# Revit family: Pump_Commercial-Effluent-Zoeller-180_Automatic_Series
name_source: partatom
category: Mechanical Equipment
revit_build: Autodesk Revit 2018 (Build: 20170223_1515(x64)
units: mm (PartAtom-declared; Revit-internal decimal feet)

## family parameters
Always vertical = No
Cut with Voids When Loaded = No
OmniClass Number = 23.60.30.21
OmniClass Title = Pumps
Part Type = Normal
Room Calculation Point = No
Round Connector Dimension = Use Radius
Shared = Yes
Work Plane-Based = Yes

## types (8) — shared parameters
Assembly Code = D2090
Cooling = Oil Filled
Cord Length = 240"
Cord Type = 1 Ph: UL listed 3-wire neoprene cord & plug
Default Elevation = 0"
Description = High Head Flow-Mate Series Submersible Effluent Pumps
Discharge Diameter = 1 1/2"
Discharge Height = 6"
Discharge Radius = 3/4"
Gasket = Neoprene square ring & gasket
Hardware = Stainless steel
Height = 19 5/16"
Hertz = 60
Impeller = Cast Iron
Impeller Type = Non-clogging vortex
Installation Type = Floor Mounted
Lead Wires Insulation = Class B
Length = 10 11/32"
Lower Bearing = Ball bearing
Manufacturer = Zoeller
Material = Cast Iron-Zoeller-Powder Coated Epoxy
Max. Operating Temp. = 130° F (54° C)
Mechanical Seals = Stainless steel, carbon and ceramic
Motor Protection = Auto Reset thermal Overload (1 Ph).
Motor Shaft = SAE 1117 carbon steel
Motor Type = Submersible
Off Point = 5 1/4"
On Point = 15 3/4"
Operation = Automatic
Phase = 1
Price = Prices may vary. Please consult Manufacturer Representative for most up-to-date price list.
Product Documentation Link = http://cdn.qleapahead.com
Product Page URL = http://www.zoellerpumps.com
RPM = 3450
Solid Handling = 3/4" Spherical Solids
Type = Permanent Split Capacitor
Type Comments = Available in single or double seal designs.
URL = http://www.zoellerpumps.com
Upper Bearing = Ball bearing
Warranty Information = 18 Months (Limited)
Waste Connection = Yes
Width = 12 3/4"

## per-type parameters (varying)
| type | Amps | Apparent Load | Flow @ 30' | Flow @ 5' | Insulation | Maximum Head | Model | Motor | Shipping Weight | Voltage |
| D185 - 230V/1Ph/9.8A/1HP | 10 A | 2254 VA | 85 GPM | 0 GPM | Class B | 876" | D185 | 1 HP | 85 lbs | 230 V |
| H185 - 200V/1Ph/11.5A/1HP | 12 A | 2300 VA | 85 GPM | 0 GPM | Class B | 876" | H185 | 1 HP | 86 lbs | 200 V |
| D186 - 230V/1Ph/13.7A/1.5HP | 14 A | 3151 VA | 58 GPM | 58 GPM | Class F | 1368" | D186 | 1.5 HP | 91 lbs | 230 V |
| H186 - 200V/1Ph/17.2A/1.5HP | 17 A | 3440 VA | 58 GPM | 58 GPM | Class F | 1368" | H186 | 1.5 HP | 91 lbs | 200 V |
| D188 - 230V/1Ph/14A/1.5HP | 14 A | 3220 VA | 116 GPM | 145 GPM | Class F | 1092" | D188 | 1.5 HP | 91 lbs | 230 V |
| H188 - 200V/1Ph/16.8A/1.5HP | 17 A | 3360 VA | 116 GPM | 145 GPM | Class F | 1092" | H188 | 1.5 HP | 91 lbs | 200 V |
| D189 - 230V/1Ph/17.1A/2HP | 17 A | 3933 VA | 120 GPM | 145 GPM | Class F | 1320" | D189 | 2 HP | 91 lbs | 230 V |
| H189 - 200V/1Ph/20.5A/2HP | 21 A | 4100 VA | 120 GPM | 145 GPM | Class F | 1320" | H189 | 2 HP | 91 lbs | 200 V |

## geometry (parser evidence)
native form markers: Sweep x3
no freeform markers — native parametric forms only
